# Revit family: monsun_r__ex_51fxc27a410a3g_85af
name_source: partatom
category: Lighting Fixtures
units: mm (PartAtom-declared; Revit-internal decimal feet)

## family parameters
Cut with Voids When Loaded = No
Host = Face
Light Source = No
Part Type = Normal
Room Calculation Point = No
Round Connector Dimension = Use Diameter
Shared = No

## types (1)
- --- (1 x LED, 1600 lm, 13 W, 4000K)
    Apparent Load = 13 VA
    CIE Flux Codes = 40 70 89 90 100
    Color Rendering = 80
    Color Temperature = 4000K
    Default Elevation = 1800 mm
    Description = Monsun® Ex, damp-proof luminaire, primary optical cover: cover, of PC, UV-stabilised, opal, light emission: direct distribution, primary light characteristic: symmetric, installation type: surface-mounted, LED, rated luminous flux: 1.600lm, luminous efficacy: 123lm/W, light colour: 840, colour temperature: 4000K, control gear: ECG, with terminal, 3+1-pole, max. 2.5mm², through-wiring: 6x 2.5mm², mains connection: 220..240V, AC, 50/60Hz, rated input power: 13W, control gear: single battery element, housing, of PC, light grey (RAL 7035), incl. 1x Ex cable gland M20 for cable diameter 7..12mm with sealing, incl. 3x Ex locking screw M20 with sealing, length: 338mm, width: 176mm, height: 110mm, clip for enclosure, of stainless steel, protection rating (complete): IP66, insulation class (complete): insulation class I (protective earthing), certification: CE, explosion class: zone 2,22 II 3G Ex nR IIC T6 GC, II3D Ex tc IIIC T65°C Dc, impact resistance: IK10, permissible operating ambient temperature: 0..+35°C, LABS conformity tested according to VDMA 24364:2018-05, contact your sales advisor before using the luminaires in applications with unclear chemical exposure, large temperature fluctuations or condensation-forming humidity, packaging unit: 1 piece
    Height = 110 mm
    Lamp = 1 x LED
    Lamp Light Flux = 1600 lm
    Lamp Power = 13 W
    Lamp count = 1
    Length = 338 mm
    Luminous efficacy = 123 lm/W
    Manufacturer = Siteco
    ModVariant = No
    Model = 51FXC27A410A3G
    Mounting Place = Ceiling
    Mounting Type = Surface mounted
    Number of Poles = 1
    OnlyDefault = Yes
    Power Factor = 1
    Product Name = Monsun® Ex
    Product group = damp-proof luminaire
    ProductGroupID = 301
    Protection Class = Protection class I
    Protection Degree = IP 66
    RLX_Detail_Level = 1
    RLX_Emergency_Light_Flux = 0 lm
    RLX_Emergency_Type = 0
    RLX_Emergency_Type_DB = No
    RlxData = <blob elided: 50785 chars, md5=1a39f2f4>
    Socket = socket
    Standby Power = 0 W
    System Light Flux = 1600 lm
    System Power = 13 W
    Type Comments = -
    Type Image = l_1258884.jpg
    URL = http://relux.com
    VarID = @adj_032279
    Voltage = 0 V
    Weight = 0.00 kg
    Width = 176 mm

## geometry (parser evidence)
native form markers: Sweep x12
no freeform markers — native parametric forms only
